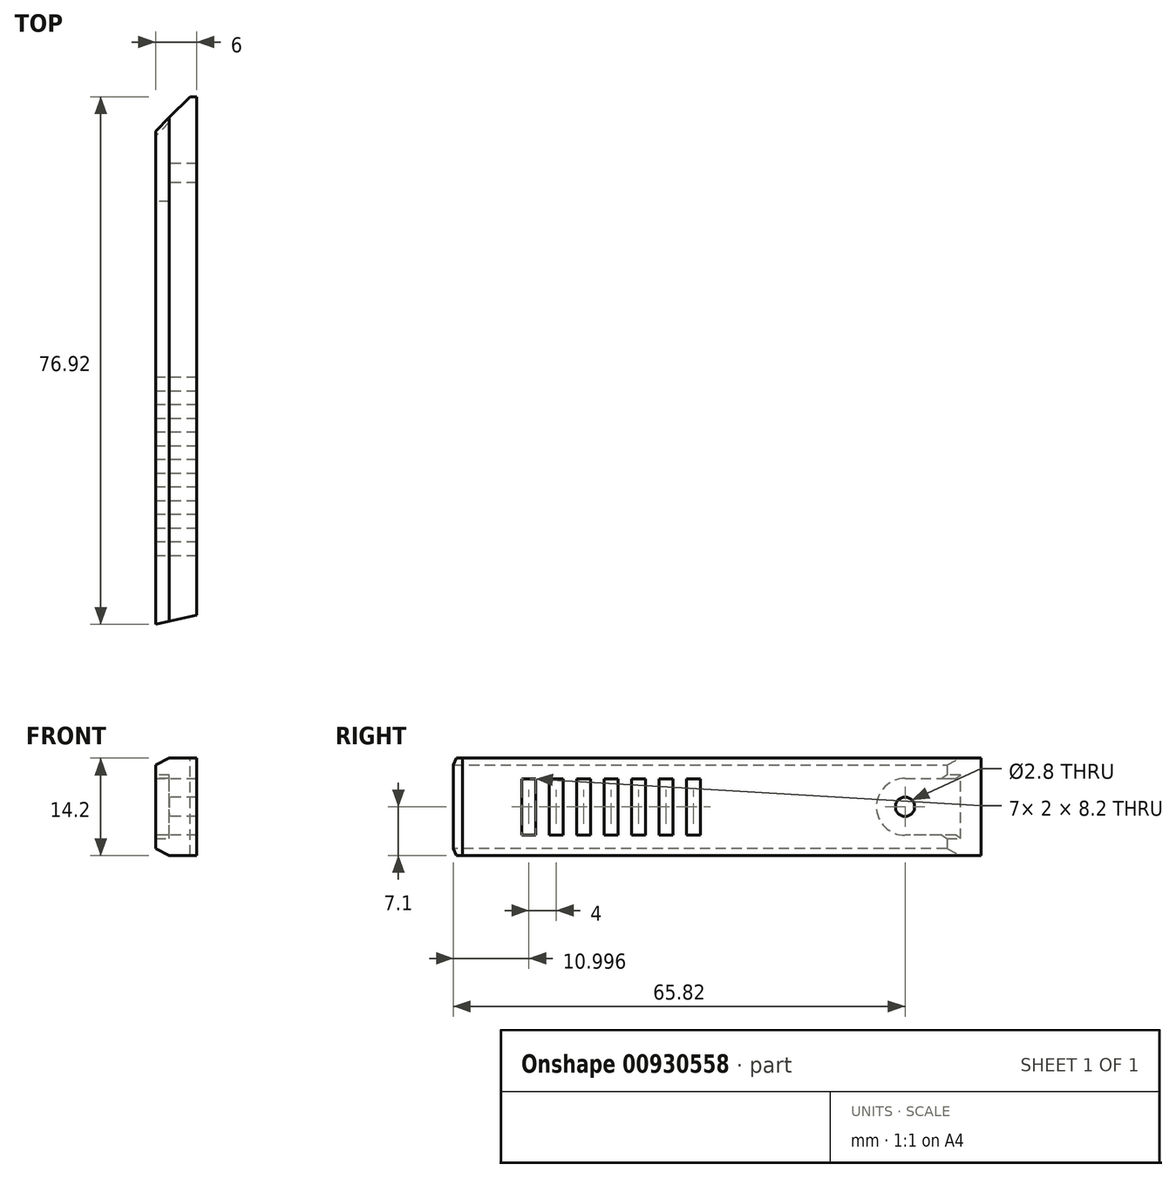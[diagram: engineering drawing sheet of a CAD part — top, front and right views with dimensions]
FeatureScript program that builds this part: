
annotation { "Feature Type Name" : "Feature", "Feature Type Description" : "" }
export const myFeature = defineFeature(function(context is Context, id is Id, definition is map)
    precondition{}
    {
        {
            var Q0;
            Q0=qCreatedBy(makeId("Right.planeOp"),FACE);
            var sketch = newSketch(context, id + "F0", { "sketchPlane" : qUnion([Q0])});
            skLineSegment(sketch, "E0.bottom", {"start": v(0, 0) * mm, "end": v(-75.9, 0) * mm, "construction": true});
            skLineSegment(sketch, "E0.top", {"start": v(0, 14.8) * mm, "end": v(-75.9, 14.8) * mm, "construction": true});
            skLineSegment(sketch, "E0.left", {"start": v(0, 0) * mm, "end": v(0, 14.8) * mm, "construction": true});
            skLineSegment(sketch, "E0.right", {"start": v(-75.9, 0) * mm, "end": v(-75.9, 14.8) * mm, "construction": true});
            skLineSegment(sketch, "E1.bottom", {"start": v(-0.3, 14.5) * mm, "end": v(-75.9, 14.5) * mm});
            skLineSegment(sketch, "E1.top", {"start": v(-0.3, 0.3) * mm, "end": v(-75.9, 0.3) * mm});
            skLineSegment(sketch, "E1.left", {"start": v(-0.3, 14.5) * mm, "end": v(-0.3, 0.3) * mm});
            skLineSegment(sketch, "E1.right", {"start": v(-75.9, 14.5) * mm, "end": v(-75.9, 0.3) * mm});
            skSolve(sketch);
        }
        {
            var Q0;
            Q0=qSketchRegion(id+"F0",true);
            extrude(context, id + "F1", {"entities" : qUnion([Q0]), "depth" : 6 * mm, "offsetDistance" : 25 * mm});
        }
        {
            var Q0;
            Q0=makeQuery(id+"F1.opExtrude","SWEPT_FACE",FACE,{"disambiguationData":[OSD([sQuery(id+"F0.wireOp",EDGE,"E1.top")])]});
            var sketch = newSketch(context, id + "F2", { "sketchPlane" : qUnion([Q0])});
            skLineSegment(sketch, "E2", {"start": v(0, 75.9) * mm, "end": v(6, 75.9) * mm});
            skLineSegment(sketch, "E3", {"start": v(6, 75.9) * mm, "end": v(0, 77.22) * mm});
            skLineSegment(sketch, "E4", {"start": v(0, 77.22) * mm, "end": v(0, 75.9) * mm});
            skSolve(sketch);
        }
        {
            var Q0;
            Q0=qSketchRegion(id+"F2",true);
            var Q1;
            Q1=makeQuery(id+"F1.opExtrude","SWEPT_FACE",FACE,{"disambiguationData":[OSD([sQuery(id+"F0.wireOp",EDGE,"E1.bottom")])]});
            extrude(context, id + "F3", {"entities" : qUnion([Q0]), "operationType" : NewBodyOperationType.ADD, "endBound" : BoundingType.UP_TO_SURFACE, "oppositeDirection" : true, "depth" : 25 * mm, "endBoundEntityFace" : qUnion([Q1]), "offsetDistance" : 25 * mm});
        }
        {
            var Q0;
            Q0=makeQuery(id+"F3.boolean.opBoolean","MERGE",EDGE,{"derivedFrom":[makeQuery(id+"F1.opExtrude","CAP_EDGE",EDGE,{"disambiguationData":[OSD([sQuery(id+"F0.wireOp",EDGE,"E1.top")])],"isStart":true}),makeQuery(id+"F3.opExtrude","CAP_EDGE",EDGE,{"disambiguationData":[OSD([sQuery(id+"F2.wireOp",EDGE,"E4")])],"isStart":true})]});
            var Q1;
            Q1=makeQuery(id+"F3.boolean.opBoolean","MERGE",EDGE,{"derivedFrom":[makeQuery(id+"F1.opExtrude","CAP_EDGE",EDGE,{"disambiguationData":[OSD([sQuery(id+"F0.wireOp",EDGE,"E1.bottom")])],"isStart":true}),makeQuery(id+"F3.opExtrude","CAP_EDGE",EDGE,{"disambiguationData":[OSD([sQuery(id+"F2.wireOp",EDGE,"E4")])],"isStart":false})]});
            chamfer(context, id + "F4", {"entities" : qUnion([Q0, Q1]), "chamferType" : ChamferType.TWO_OFFSETS, "width1" : 1 * mm, "oppositeDirection" : false, "width2" : 2 * mm, "tangentPropagation" : true});
        }
        {
            var Q0;
            Q0=makeQuery(id+"F1.opExtrude","CAP_EDGE",EDGE,{"disambiguationData":[OSD([sQuery(id+"F0.wireOp",EDGE,"E1.left")])],"isStart":true});
            chamfer(context, id + "F5", {"entities" : qUnion([Q0]), "chamferType" : ChamferType.TWO_OFFSETS, "width1" : 5 * mm, "oppositeDirection" : false, "width2" : 5 * mm, "tangentPropagation" : true});
        }
        {
            var Q0;
            Q0=makeQuery(id+"F3.boolean.opBoolean","MERGE",FACE,{"derivedFrom":[makeQuery(id+"F1.opExtrude","CAP_FACE",FACE,{"disambiguationData":[OSD([sQuery(id+"F0.wireOp",EDGE,"E1.bottom"),sQuery(id+"F0.wireOp",EDGE,"E1.top"),sQuery(id+"F0.wireOp",EDGE,"E1.left"),sQuery(id+"F0.wireOp",EDGE,"E1.right")])],"isStart":true}),makeQuery(id+"F3.opExtrude","SWEPT_FACE",FACE,{"disambiguationData":[OSD([sQuery(id+"F2.wireOp",EDGE,"E4")])]})]});
            var sketch = newSketch(context, id + "F6", { "sketchPlane" : qUnion([Q0])});
            skLineSegment(sketch, "E5.bottom", {"start": v(41.22, 11.5) * mm, "end": v(43.22, 11.5) * mm});
            skLineSegment(sketch, "E5.top", {"start": v(41.22, 3.3) * mm, "end": v(43.22, 3.3) * mm});
            skLineSegment(sketch, "E5.left", {"start": v(41.22, 11.5) * mm, "end": v(41.22, 3.3) * mm});
            skLineSegment(sketch, "E5.right", {"start": v(67.22, 11.5) * mm, "end": v(67.22, 3.3) * mm});
            skLineSegment(sketch, "E6", {"start": v(43.22, 11.5) * mm, "end": v(43.22, 3.3) * mm});
            skLineSegment(sketch, "E7", {"start": v(45.22, 11.5) * mm, "end": v(45.22, 3.3) * mm});
            skLineSegment(sketch, "E8", {"start": v(47.22, 11.5) * mm, "end": v(47.22, 3.3) * mm});
            skLineSegment(sketch, "E9", {"start": v(49.22, 11.5) * mm, "end": v(49.22, 3.3) * mm});
            skLineSegment(sketch, "E10", {"start": v(51.22, 11.5) * mm, "end": v(51.22, 3.3) * mm});
            skLineSegment(sketch, "E11", {"start": v(53.22, 11.5) * mm, "end": v(53.22, 3.3) * mm});
            skLineSegment(sketch, "E12", {"start": v(57.22, 11.5) * mm, "end": v(57.22, 3.3) * mm});
            skLineSegment(sketch, "E13", {"start": v(59.22, 11.5) * mm, "end": v(59.22, 3.3) * mm});
            skLineSegment(sketch, "E14", {"start": v(61.22, 11.5) * mm, "end": v(61.22, 3.3) * mm});
            skLineSegment(sketch, "E15", {"start": v(63.22, 11.5) * mm, "end": v(63.22, 3.3) * mm});
            skLineSegment(sketch, "E16", {"start": v(65.22, 11.5) * mm, "end": v(65.22, 3.3) * mm});
            skLineSegment(sketch, "E17", {"start": v(55.22, 11.5) * mm, "end": v(55.22, 3.3) * mm});
            skLineSegment(sketch, "E18.trimOffspring", {"start": v(45.22, 11.5) * mm, "end": v(47.22, 11.5) * mm});
            skLineSegment(sketch, "E19.trimOffspring", {"start": v(45.22, 3.3) * mm, "end": v(47.22, 3.3) * mm});
            skLineSegment(sketch, "E20.trimOffspring", {"start": v(49.22, 11.5) * mm, "end": v(51.22, 11.5) * mm});
            skLineSegment(sketch, "E21.trimOffspring", {"start": v(49.22, 3.3) * mm, "end": v(51.22, 3.3) * mm});
            skLineSegment(sketch, "E22.trimOffspring", {"start": v(53.22, 11.5) * mm, "end": v(55.22, 11.5) * mm});
            skLineSegment(sketch, "E23.trimOffspring", {"start": v(53.22, 3.3) * mm, "end": v(55.22, 3.3) * mm});
            skLineSegment(sketch, "E24.trimOffspring", {"start": v(57.22, 11.5) * mm, "end": v(59.22, 11.5) * mm});
            skLineSegment(sketch, "E25.trimOffspring", {"start": v(57.22, 3.3) * mm, "end": v(59.22, 3.3) * mm});
            skLineSegment(sketch, "E26.trimOffspring", {"start": v(61.22, 11.5) * mm, "end": v(63.22, 11.5) * mm});
            skLineSegment(sketch, "E27.trimOffspring", {"start": v(61.22, 3.3) * mm, "end": v(63.22, 3.3) * mm});
            skLineSegment(sketch, "E28.trimOffspring", {"start": v(65.22, 11.5) * mm, "end": v(67.22, 11.5) * mm});
            skLineSegment(sketch, "E29.trimOffspring", {"start": v(65.22, 3.3) * mm, "end": v(67.22, 3.3) * mm});
            skLineSegment(sketch, "E30", {"start": v(43.22, 11.5) * mm, "end": v(45.22, 11.5) * mm, "construction": true});
            skLineSegment(sketch, "E31", {"start": v(47.22, 11.5) * mm, "end": v(49.22, 11.5) * mm, "construction": true});
            skLineSegment(sketch, "E32", {"start": v(51.22, 11.5) * mm, "end": v(53.22, 11.5) * mm, "construction": true});
            skLineSegment(sketch, "E33", {"start": v(55.22, 11.5) * mm, "end": v(57.22, 11.5) * mm, "construction": true});
            skLineSegment(sketch, "E34", {"start": v(59.22, 11.5) * mm, "end": v(61.22, 11.5) * mm, "construction": true});
            skLineSegment(sketch, "E35", {"start": v(63.22, 11.5) * mm, "end": v(65.22, 11.5) * mm, "construction": true});
            skSolve(sketch);
        }
        {
            var Q0;
            Q0=qSketchRegion(id+"F6",true);
            extrude(context, id + "F7", {"entities" : qUnion([Q0]), "operationType" : NewBodyOperationType.REMOVE, "endBound" : BoundingType.UP_TO_NEXT, "oppositeDirection" : true, "depth" : 25 * mm, "offsetDistance" : 25 * mm});
        }
        {
            var Q0;
            Q0=makeQuery(id+"F3.boolean.opBoolean","MERGE",FACE,{"derivedFrom":[makeQuery(id+"F1.opExtrude","CAP_FACE",FACE,{"disambiguationData":[OSD([sQuery(id+"F0.wireOp",EDGE,"E1.bottom"),sQuery(id+"F0.wireOp",EDGE,"E1.top"),sQuery(id+"F0.wireOp",EDGE,"E1.left"),sQuery(id+"F0.wireOp",EDGE,"E1.right")])],"isStart":true}),makeQuery(id+"F3.opExtrude","SWEPT_FACE",FACE,{"disambiguationData":[OSD([sQuery(id+"F2.wireOp",EDGE,"E4")])]})]});
            var sketch = newSketch(context, id + "F8", { "sketchPlane" : qUnion([Q0])});
            skArc(sketch, "E36", {"start": v(11.4, 3.25) * mm, "mid": v(15.55, 7.4) * mm, "end": v(11.4, 11.55) * mm});
            skLineSegment(sketch, "E37", {"start": v(11.4, 7.4) * mm, "end": v(11.4, 13.5) * mm, "construction": true});
            skLineSegment(sketch, "E38", {"start": v(11.4, 7.4) * mm, "end": v(11.4, 1.3) * mm, "construction": true});
            skLineSegment(sketch, "E39", {"start": v(11.4, 7.4) * mm, "end": v(5.3, 7.4) * mm, "construction": true});
            skLineSegment(sketch, "E40", {"start": v(11.4, 11.55) * mm, "end": v(0.3, 11.55) * mm});
            skLineSegment(sketch, "E41", {"start": v(0.3, 11.55) * mm, "end": v(0.3, 3.25) * mm});
            skLineSegment(sketch, "E42", {"start": v(0.3, 3.25) * mm, "end": v(11.4, 3.25) * mm});
            skSolve(sketch);
        }
        {
            var Q0;
            Q0=qSketchRegion(id+"F8",true);
            extrude(context, id + "F9", {"entities" : qUnion([Q0]), "operationType" : NewBodyOperationType.REMOVE, "oppositeDirection" : true, "depth" : 2 * mm, "offsetDistance" : 25 * mm});
        }
        {
            var Q0;
            Q0=makeQuery(id+"F9.boolean.opBoolean","INTERSECT",EDGE,{"derivedFrom":[makeQuery(id+"F5.opChamfer","BLEND_FACE",FACE,{"disambiguationData":[OSD([sQuery(id+"F0.wireOp",EDGE,"E1.left")])]}),makeQuery(id+"F9.opExtrude","SWEPT_FACE",FACE,{"disambiguationData":[OSD([sQuery(id+"F8.wireOp",EDGE,"E40")])]})]});
            var Q1;
            Q1=makeQuery(id+"F9.boolean.opBoolean","COPY",EDGE,{"derivedFrom":makeQuery(id+"F9.opExtrude","CAP_EDGE",EDGE,{"disambiguationData":[OSD([sQuery(id+"F8.wireOp",EDGE,"E40")])],"isStart":true})});
            var Q2;
            Q2=makeQuery(id+"F9.boolean.opBoolean","INTERSECT",EDGE,{"derivedFrom":[makeQuery(id+"F5.opChamfer","BLEND_FACE",FACE,{"disambiguationData":[OSD([sQuery(id+"F0.wireOp",EDGE,"E1.left")])]}),makeQuery(id+"F9.opExtrude","SWEPT_FACE",FACE,{"disambiguationData":[OSD([sQuery(id+"F8.wireOp",EDGE,"E42")])]})]});
            chamfer(context, id + "F10", {"entities" : qUnion([Q0, Q1, Q2]), "width" : 0.5 * mm, "tangentPropagation" : true});
        }
        {
            var Q0;
            Q0=makeQuery(id+"F9.boolean.opBoolean","COPY",FACE,{"derivedFrom":makeQuery(id+"F9.opExtrude","CAP_FACE",FACE,{"disambiguationData":[OSD([sQuery(id+"F8.wireOp",EDGE,"E36"),sQuery(id+"F8.wireOp",EDGE,"E40"),sQuery(id+"F8.wireOp",EDGE,"E41"),sQuery(id+"F8.wireOp",EDGE,"E42")])],"isStart":false})});
            var sketch = newSketch(context, id + "F11", { "sketchPlane" : qUnion([Q0])});
            skCircle(sketch, "E43", {"center": v(11.4, 7.4) * mm, "radius": 1.4 * mm});
            skSolve(sketch);
        }
        {
            var Q0;
            Q0=qSketchRegion(id+"F11",true);
            extrude(context, id + "F12", {"entities" : qUnion([Q0]), "operationType" : NewBodyOperationType.REMOVE, "endBound" : BoundingType.UP_TO_NEXT, "oppositeDirection" : true, "depth" : 25 * mm, "offsetDistance" : 25 * mm});
        }
    });
